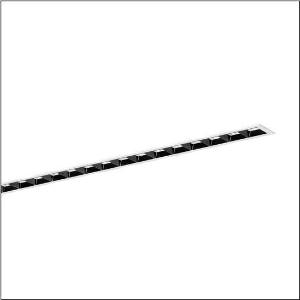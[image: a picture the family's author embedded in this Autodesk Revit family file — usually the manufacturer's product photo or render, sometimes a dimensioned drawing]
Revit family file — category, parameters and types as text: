
# Revit family: silica_r__21_51mx12db45wb_7f54
name_source: partatom
category: Lighting Fixtures
units: mm (PartAtom-declared; Revit-internal decimal feet)

## family parameters
Cut with Voids When Loaded = No
Host = Face
Light Source = No
Part Type = Normal
Room Calculation Point = No
Round Connector Dimension = Use Diameter
Shared = No

## types (1)
- --- (1 x LED, 5400 lm, 32 W, 4000K)
    Apparent Load = 32 VA
    CIE Flux Codes = 86 100 100 100 100
    Color Rendering = 80
    Color Temperature = 4000K
    Default Elevation = 1800 mm
    Description = Silica® 21, office luminaire, primary light control with darklight reflector, of PMMA, black, CAT 2 (L<= 3000cd/m²), light emission: direct distribution, primary light characteristic: symmetric, installation type: recessed, LED, rated luminous flux: 5.400lm, luminous efficacy: 169lm/W, light colour: 840, colour temperature: 4000K, with terminal, 3+2-pole, max. 2.5mm², mains connection: 220..240V, AC, 50/60Hz, rated input power: 32W, luminaire housing, of aluminium, traffic white (RAL 9016), length: 1.528mm, width: 79mm, height: 53mm, protection rating (complete): IP20, insulation class (complete): insulation class I (protective earthing), certification: CE, permissible operating ambient temperature: 0..+35°C, standard: EN 50419, packaging unit: 1 piece
    Height = 0 mm  [stored 0 ft]
    Lamp = 1 x LED
    Lamp Light Flux = 5400 lm
    Lamp Power = 32 W
    Lamp count = 1
    Length = 1527 mm
    Luminous efficacy = 169 lm/W
    Manufacturer = Siteco
    ModVariant = No
    Model = 51MX12DB45WB
    Mounting Place = Ceiling
    Mounting Type = Recessed
    Number of Poles = 1
    OnlyDefault = Yes
    Power Factor = 1
    Product Name = Silica® 21
    Product group = office luminaire | ceiling recessed
    ProductGroupID = 401
    Protection Class = Protection class I
    Protection Degree = IP 20
    RLX_Detail_Level = 1
    RLX_Emergency_Light_Flux = 0 lm
    RLX_Emergency_Type = 0
    RLX_Emergency_Type_DB = No
    RlxData = <blob elided: 42257 chars, md5=fd69f840>
    Socket = socket
    Standby Power = 0 W
    System Light Flux = 5400 lm
    System Power = 32 W
    Type Comments = factory setting: luminous flux: 100 % | dim-lin: 254 | 366 mA
    Type Image = l_1313610.jpg
    URL = http://relux.com
    VarID = @adj_073819
    Voltage = 0 V
    Weight = 0.00 kg
    Width = 79 mm

note: [stored X ft] marks values corroborated as IEEE doubles in the binary element streams (Revit-internal decimal feet)

## geometry (parser evidence)
native form markers: Blend x4, Sweep x11
no freeform markers — native parametric forms only
